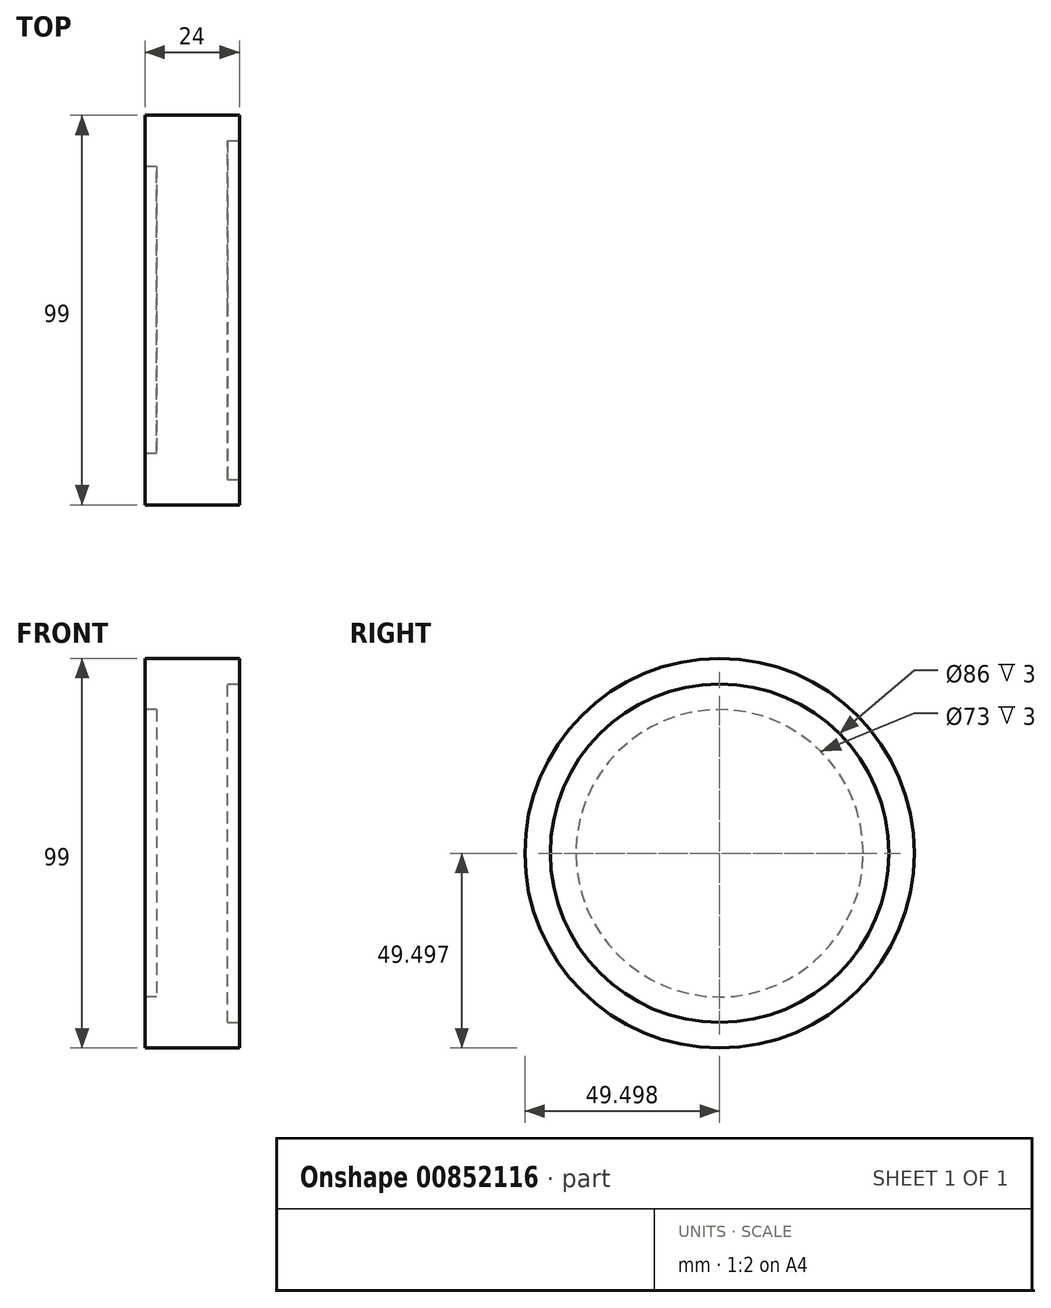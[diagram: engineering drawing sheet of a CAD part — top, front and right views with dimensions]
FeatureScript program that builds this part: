
annotation { "Feature Type Name" : "Feature", "Feature Type Description" : "" }
export const myFeature = defineFeature(function(context is Context, id is Id, definition is map)
    precondition{}
    {
        {
            var Q0;
            Q0=qCreatedBy(makeId("Right.planeOp"),FACE);
            var sketch = newSketch(context, id + "F0", { "sketchPlane" : qUnion([Q0])});
            skCircle(sketch, "E0", {"center": v(-14.71, 24.09) * mm, "radius": 49.5 * mm});
            skSolve(sketch);
        }
        {
            var Q0;
            Q0=makeQuery(id+"F0.imprint","IMPRINT",FACE,{"disambiguationData":[TD([[makeQuery(id+"F0.imprint","IMPRINT",EDGE,{"derivedFrom":sQuery(id+"F0.wireOp",EDGE,"E0")}),1.0]])]});
            extrude(context, id + "F1", {"entities" : qUnion([Q0]), "depth" : 24 * mm, "offsetDistance" : 25.4 * mm});
        }
        {
            var Q0;
            Q0=makeQuery(id+"F1.opExtrude","CAP_FACE",FACE,{"disambiguationData":[OSD([sQuery(id+"F0.wireOp",EDGE,"E0")])],"isStart":false});
            var sketch = newSketch(context, id + "F2", { "sketchPlane" : qUnion([Q0])});
            skCircle(sketch, "E1", {"center": v(-14.71, 24.09) * mm, "radius": 43 * mm});
            skSolve(sketch);
        }
        {
            var Q0;
            Q0=makeQuery(id+"F2.imprint","IMPRINT",FACE,{"disambiguationData":[TD([[makeQuery(id+"F2.imprint","IMPRINT",EDGE,{"derivedFrom":sQuery(id+"F2.wireOp",EDGE,"E1")}),1.0]])]});
            extrude(context, id + "F3", {"entities" : qUnion([Q0]), "operationType" : NewBodyOperationType.REMOVE, "oppositeDirection" : true, "depth" : 3 * mm, "offsetDistance" : 25.4 * mm});
        }
        {
            var Q0;
            Q0=makeQuery(id+"F1.opExtrude","CAP_FACE",FACE,{"disambiguationData":[OSD([sQuery(id+"F0.wireOp",EDGE,"E0")])],"isStart":true});
            var sketch = newSketch(context, id + "F4", { "sketchPlane" : qUnion([Q0])});
            skCircle(sketch, "E2", {"center": v(14.71, 24.09) * mm, "radius": 36.5 * mm});
            skSolve(sketch);
        }
        {
            var Q0;
            Q0=makeQuery(id+"F4.imprint","IMPRINT",FACE,{"disambiguationData":[TD([[makeQuery(id+"F4.imprint","IMPRINT",EDGE,{"derivedFrom":sQuery(id+"F4.wireOp",EDGE,"E2")}),1.0]])]});
            extrude(context, id + "F5", {"entities" : qUnion([Q0]), "operationType" : NewBodyOperationType.REMOVE, "oppositeDirection" : true, "depth" : 3 * mm, "offsetDistance" : 25.4 * mm});
        }
    });
